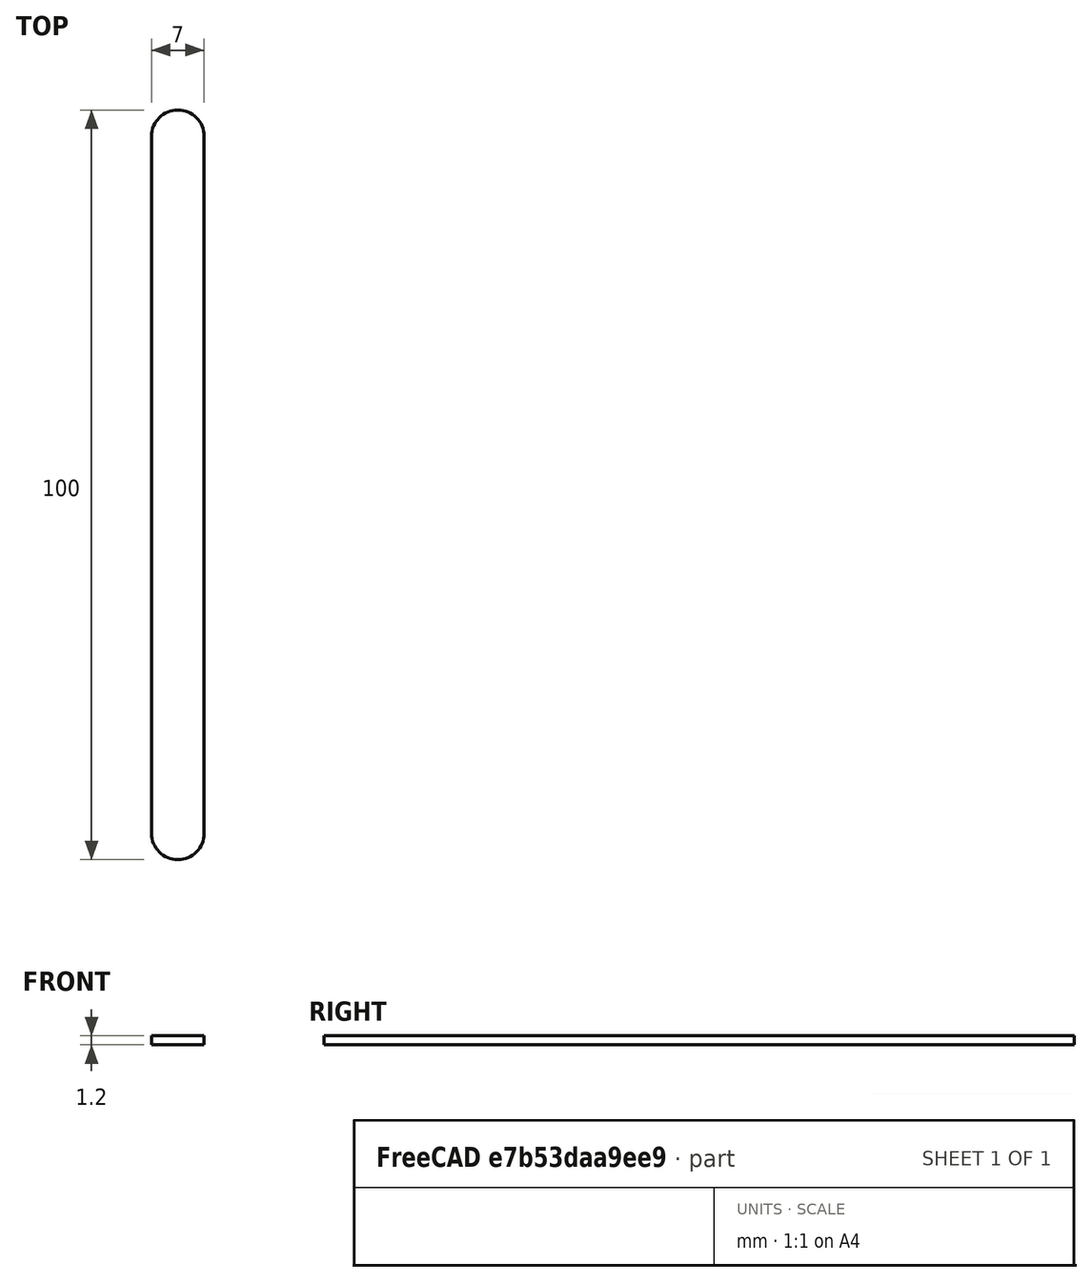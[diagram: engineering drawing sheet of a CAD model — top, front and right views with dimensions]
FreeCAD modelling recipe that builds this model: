
FCSTD DOCUMENT  (FreeCAD 0.20R29177 (Git))
Label: MixingStick (100x7x1.2)
License: All rights reserved
LicenseURL: http://en.wikipedia.org/wiki/All_rights_reserved
objects: Sketcher::SketchObject×1, Part::Face×1, Part::Extrusion×1
note: 3 computed .brp shape members not serialized (recipe doc carries the construction recipe); baked Part::Feature solids carry a one-line shape summary decoded from their .brp

FEATURE [Sketcher::SketchObject] Sketch
  FullyConstrained = false
  sketch-geometry (4):
    g0: LineSegment StartX=20.2035 StartY=129.881 StartZ=0 EndX=20.2035 EndY=36.8812 EndZ=0
    g1: LineSegment StartX=13.2035 StartY=36.8812 StartZ=0 EndX=13.2035 EndY=129.881 EndZ=0
    g2: ArcOfCircle CenterX=16.7035 CenterY=36.8812 CenterZ=0 NormalX=0 NormalY=0 NormalZ=1 AngleXU=0 Radius=3.5 StartAngle=3.14159 EndAngle=6.28319
    g3: ArcOfCircle CenterX=16.7035 CenterY=129.881 CenterZ=0 NormalX=0 NormalY=0 NormalZ=1 AngleXU=0 Radius=3.5 StartAngle=1.8e-15 EndAngle=3.14159
  constraints (14):
    c: Vertical(g0)
    c: Vertical(g1)
    c: Coincident(g2,g0)
    c: DistanceX(g1,g0) = 7
    c: Coincident(g1,g3)
    c: Coincident(g0,g3)
    c: Horizontal(g3,g1)
    c: Horizontal(g1,g0)
    c: Coincident(g1,g2)
    c: Horizontal(g0,g1)
    c: Horizontal(g1,g2)
    c: Horizontal(g2,g2)
    c: Horizontal(g2,g2)
    c: DistanceY(g2,g3) = 93
FEATURE [Part::Face] Face
  FaceMakerClass = Part::FaceMakerBullseye
  Sources = -> [Sketch]
FEATURE [Part::Extrusion] Extrude
  Base = -> Sketch
  Dir = (0,0,1)
  DirMode = 2
  FaceMakerClass = Part::FaceMakerBullseye
  LengthFwd = 1.2
  LengthRev = 0
  Solid = true
  Symmetric = false
